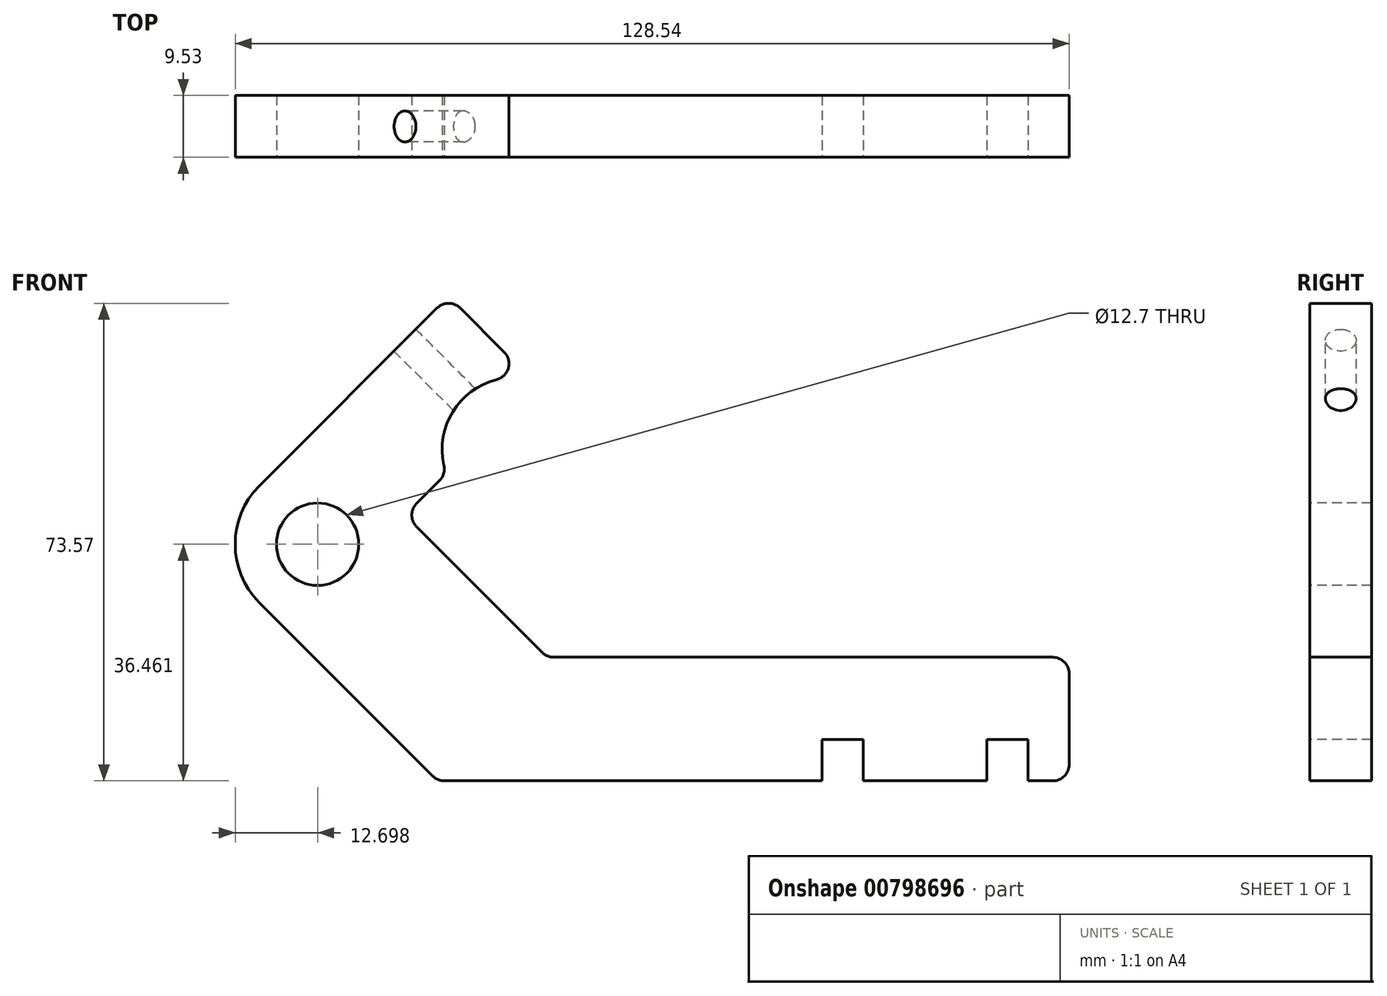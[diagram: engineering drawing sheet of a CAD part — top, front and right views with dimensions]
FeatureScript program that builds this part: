
annotation { "Feature Type Name" : "Feature", "Feature Type Description" : "" }
export const myFeature = defineFeature(function(context is Context, id is Id, definition is map)
    precondition{}
    {
        {
            var Q0;
            Q0=qCreatedBy(makeId("Front.planeOp"),FACE);
            var sketch = newSketch(context, id + "F0", { "sketchPlane" : qUnion([Q0])});
            skArc(sketch, "E0", {"start": v(33.41, 24.39) * mm, "mid": v(22.5, 21.07) * mm, "end": v(20.26, 9.87) * mm});
            skLineSegment(sketch, "E1", {"start": v(30.73, 13.6) * mm, "end": v(4.61, 13.6) * mm, "construction": true});
            skLineSegment(sketch, "E2", {"start": v(30.73, 13.6) * mm, "end": v(13.89, 30.44) * mm, "construction": true});
            skLineSegment(sketch, "E3.0", {"start": v(33.41, 24.39) * mm, "end": v(20.62, 37.18) * mm});
            skLineSegment(sketch, "E4", {"start": v(22.87, 21.46) * mm, "end": v(-8.56, -9.97) * mm, "construction": true});
            skLineSegment(sketch, "E5.0", {"start": v(4.9, -5.48) * mm, "end": v(-4.28, 3.71) * mm, "construction": true});
            skCircle(sketch, "E6", {"center": v(0.42, -0.99) * mm, "radius": 6.35 * mm});
            skLineSegment(sketch, "E7.0", {"start": v(20.62, 37.18) * mm, "end": v(-8.56, 8) * mm});
            skLineSegment(sketch, "E8.0", {"start": v(35.8, -18.4) * mm, "end": v(13.89, 3.5) * mm});
            skLineSegment(sketch, "E9.0", {"start": v(18.92, -37.45) * mm, "end": v(-8.56, -9.97) * mm});
            skLineSegment(sketch, "E10.0", {"start": v(20.26, 9.87) * mm, "end": v(13.89, 3.5) * mm});
            skLineSegment(sketch, "E11", {"start": v(9.4, -27.93) * mm, "end": v(116.26, -27.93) * mm, "construction": true});
            skLineSegment(sketch, "E12.0", {"start": v(26.27, -8.88) * mm, "end": v(116.26, -8.88) * mm, "construction": true});
            skLineSegment(sketch, "E13.0", {"start": v(52.76, -27.93) * mm, "end": v(52.76, -8.88) * mm, "construction": true});
            skArc(sketch, "E14.trimOffspring", {"start": v(-8.56, 8) * mm, "mid": v(-12.28, -0.99) * mm, "end": v(-8.56, -9.97) * mm});
            skLineSegment(sketch, "E15.0", {"start": v(116.26, -37.45) * mm, "end": v(116.26, -18.4) * mm});
            skLineSegment(sketch, "E16.bottom", {"start": v(109.9, -8.88) * mm, "end": v(103.56, -8.88) * mm, "construction": true});
            skLineSegment(sketch, "E16.top", {"start": v(109.9, -15.23) * mm, "end": v(103.56, -15.23) * mm, "construction": true});
            skLineSegment(sketch, "E16.left", {"start": v(109.9, -31.1) * mm, "end": v(109.9, -37.45) * mm});
            skLineSegment(sketch, "E16.right", {"start": v(103.56, -31.1) * mm, "end": v(103.56, -37.45) * mm});
            skLineSegment(sketch, "E17.bottom", {"start": v(78.16, -8.88) * mm, "end": v(84.5, -8.88) * mm, "construction": true});
            skLineSegment(sketch, "E17.top", {"start": v(78.16, -15.23) * mm, "end": v(84.5, -15.23) * mm, "construction": true});
            skLineSegment(sketch, "E17.left", {"start": v(78.16, -31.1) * mm, "end": v(78.16, -37.45) * mm});
            skLineSegment(sketch, "E17.right", {"start": v(84.5, -31.1) * mm, "end": v(84.5, -37.45) * mm});
            skLineSegment(sketch, "E18.0", {"start": v(78.16, -31.1) * mm, "end": v(84.5, -31.1) * mm});
            skLineSegment(sketch, "E19.0", {"start": v(18.92, -37.45) * mm, "end": v(116.26, -37.45) * mm});
            skLineSegment(sketch, "E20.0", {"start": v(35.8, -18.4) * mm, "end": v(116.26, -18.4) * mm});
            skLineSegment(sketch, "E21", {"start": v(103.56, -31.1) * mm, "end": v(109.9, -31.1) * mm});
            skLineSegment(sketch, "E22", {"start": v(116.26, -18.4) * mm, "end": v(116.26, -8.88) * mm, "construction": true});
            skSolve(sketch);
        }
        {
            var Q0;
            Q0=makeQuery(id+"F0.imprint","IMPRINT",FACE,{"disambiguationData":[TD([[makeQuery(id+"F0.imprint","IMPRINT",EDGE,{"derivedFrom":sQuery(id+"F0.wireOp",EDGE,"E0")}),-1.0]])]});
            extrude(context, id + "F1", {"entities" : qUnion([Q0]), "oppositeDirection" : true, "depth" : 9.52 * mm, "offsetDistance" : 25.4 * mm});
        }
        {
            var Q0;
            Q0=makeQuery(id+"F1.opExtrude","SWEPT_FACE",FACE,{"disambiguationData":[OSD([sQuery(id+"F0.wireOp",EDGE,"E7.0")])]});
            var sketch = newSketch(context, id + "F2", { "sketchPlane" : qUnion([Q0])});
            skCircle(sketch, "E23", {"center": v(-4.76, 31.35) * mm, "radius": 2.38 * mm});
            skSolve(sketch);
        }
        {
            var Q0;
            Q0=makeQuery(id+"F2.imprint","IMPRINT",FACE,{"disambiguationData":[TD([[makeQuery(id+"F2.imprint","IMPRINT",EDGE,{"derivedFrom":sQuery(id+"F2.wireOp",EDGE,"E23")}),1.0]])]});
            extrude(context, id + "F3", {"entities" : qUnion([Q0]), "operationType" : NewBodyOperationType.REMOVE, "oppositeDirection" : true, "depth" : 25.4 * mm, "offsetDistance" : 25.4 * mm});
        }
        {
            var Q0;
            Q0=makeQuery(id+"F1.opExtrude","SWEPT_EDGE",EDGE,{"disambiguationData":[OSD([sQuery(id+"F0.wireOp",EDGE,"E0"),sQuery(id+"F0.wireOp",EDGE,"E3.0")])]});
            var Q1;
            Q1=makeQuery(id+"F1.opExtrude","SWEPT_EDGE",EDGE,{"disambiguationData":[OSD([sQuery(id+"F0.wireOp",EDGE,"E0"),sQuery(id+"F0.wireOp",EDGE,"E10.0")])]});
            fillet(context, id + "F4", {"entities" : qUnion([Q0, Q1]), "radius" : 2.54 * mm, "tangentPropagation" : true, "allowEdgeOverflow" : false});
        }
        {
            var Q0;
            Q0=makeQuery(id+"F1.opExtrude","SWEPT_EDGE",EDGE,{"disambiguationData":[OSD([sQuery(id+"F0.wireOp",EDGE,"E8.0"),sQuery(id+"F0.wireOp",EDGE,"E10.0")])]});
            var Q1;
            Q1=makeQuery(id+"F1.opExtrude","SWEPT_EDGE",EDGE,{"disambiguationData":[OSD([sQuery(id+"F0.wireOp",EDGE,"E8.0"),sQuery(id+"F0.wireOp",EDGE,"E20.0")])]});
            var Q2;
            Q2=makeQuery(id+"F1.opExtrude","SWEPT_EDGE",EDGE,{"disambiguationData":[OSD([sQuery(id+"F0.wireOp",EDGE,"E9.0"),sQuery(id+"F0.wireOp",EDGE,"E19.0")])]});
            var Q3;
            Q3=makeQuery(id+"F1.opExtrude","SWEPT_EDGE",EDGE,{"disambiguationData":[OSD([sQuery(id+"F0.wireOp",EDGE,"E15.0"),sQuery(id+"F0.wireOp",EDGE,"E20.0")])]});
            var Q4;
            Q4=makeQuery(id+"F1.opExtrude","SWEPT_EDGE",EDGE,{"disambiguationData":[OSD([sQuery(id+"F0.wireOp",EDGE,"E15.0"),sQuery(id+"F0.wireOp",EDGE,"E19.0")])]});
            var Q5;
            Q5=makeQuery(id+"F1.opExtrude","SWEPT_EDGE",EDGE,{"disambiguationData":[OSD([sQuery(id+"F0.wireOp",EDGE,"E3.0"),sQuery(id+"F0.wireOp",EDGE,"E7.0")])]});
            fillet(context, id + "F5", {"entities" : qUnion([Q0, Q1, Q2, Q3, Q4, Q5]), "radius" : 2.54 * mm, "tangentPropagation" : true, "allowEdgeOverflow" : false});
        }
    });
